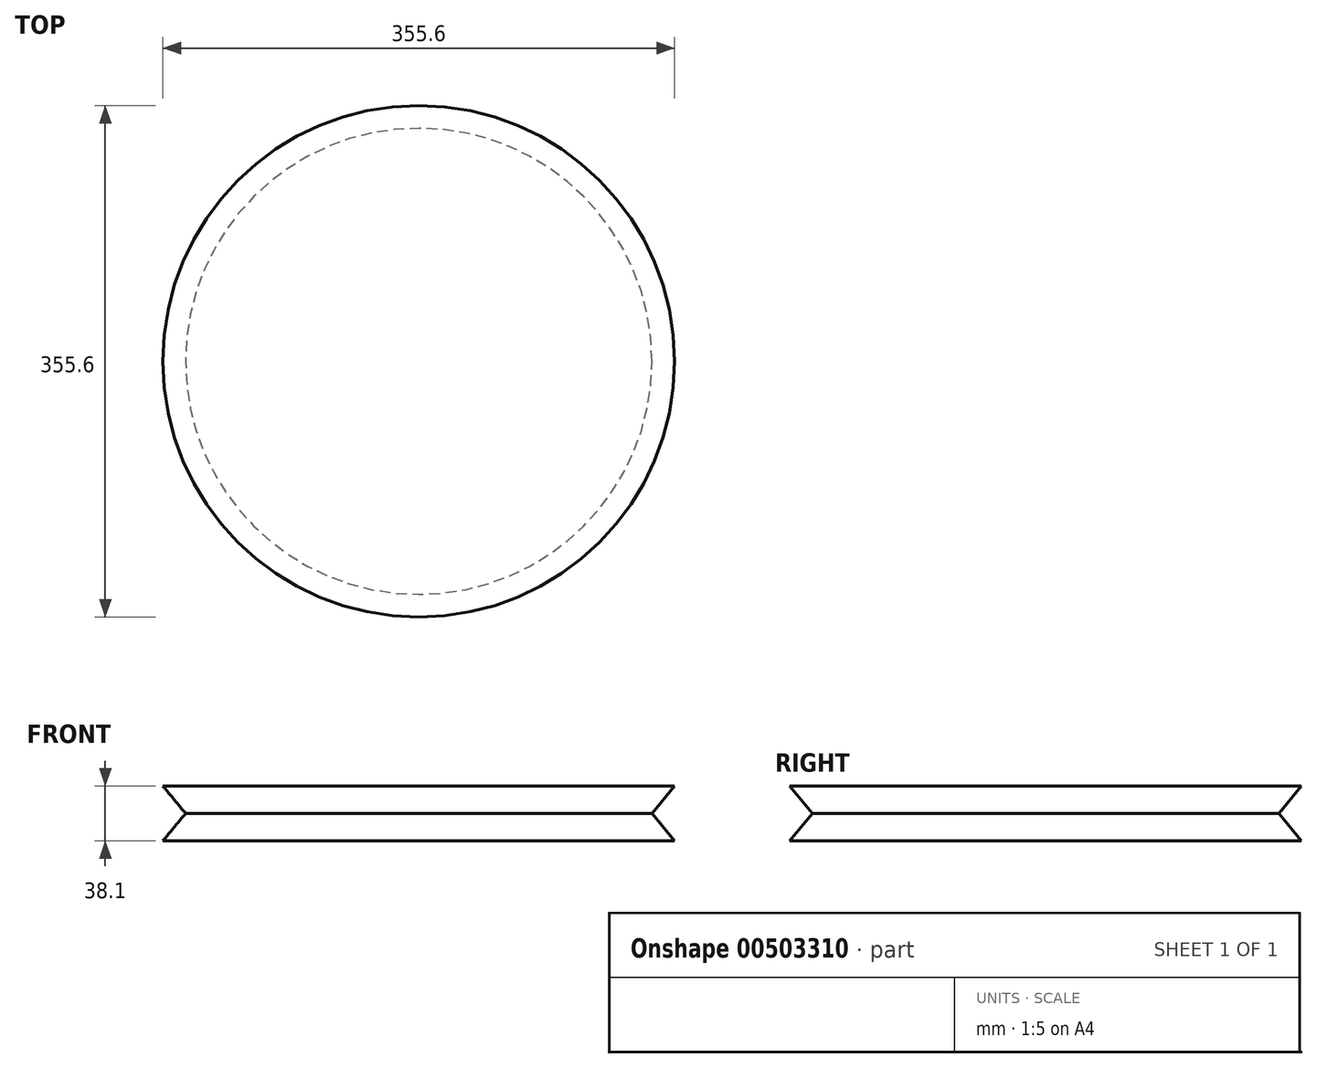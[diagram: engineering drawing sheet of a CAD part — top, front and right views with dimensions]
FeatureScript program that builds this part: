
annotation { "Feature Type Name" : "Feature", "Feature Type Description" : "" }
export const myFeature = defineFeature(function(context is Context, id is Id, definition is map)
    precondition{}
    {
        {
            var Q0;
            Q0=qCreatedBy(makeId("Front.planeOp"),FACE);
            var sketch = newSketch(context, id + "F0", { "sketchPlane" : qUnion([Q0])});
            skLineSegment(sketch, "E0", {"start": v(0, 19.05) * mm, "end": v(0, -19.05) * mm});
            skLineSegment(sketch, "E1", {"start": v(0, 19.05) * mm, "end": v(177.8, 19.05) * mm});
            skLineSegment(sketch, "E2", {"start": v(0, -19.05) * mm, "end": v(177.8, -19.05) * mm});
            skLineSegment(sketch, "E3", {"start": v(177.8, 19.05) * mm, "end": v(162.02, 0) * mm});
            skLineSegment(sketch, "E4", {"start": v(162.02, 0) * mm, "end": v(177.8, -19.05) * mm});
            skSolve(sketch);
        }
        {
            var Q0;
            Q0=qCreatedBy(makeId("Top.planeOp"),FACE);
            var sketch = newSketch(context, id + "F1", { "sketchPlane" : qUnion([Q0])});
            skCircle(sketch, "E5", {"center": v(0, 0) * mm, "radius": 177.8 * mm, "construction": true});
            skSolve(sketch);
        }
        {
            var Q0;
            Q0 = qSketchRegion(id + "F0", true);
            var Q1;
            Q1=sQuery(id+"F1.wireOp",EDGE,"E5");
            revolve(context, id + "F2", {"entities" : qUnion([Q0]), "axis" : qUnion([Q1]), "revolveType" : RevolveType.FULL});
        }
    });
